# Revit family: REEDEN 3W_LZ68G14WW
name_source: partatom
category: Luminarias
units: mm (PartAtom-declared; Revit-internal decimal feet)

## family parameters
Compartido = No
Corte con vacíos al cargar = No
Cota de conector redondo = Diámetro de uso
Origen de luz = Sí
Punto de cálculo de habitación = No
Se basa en plano de trabajo = Sí
Siempre vertical = No
Tipo de pieza = Normal

## types (1)
- REEDEN 3W_LZ68G14WW
    Cambio de temperatura de color de luz atenuada = <Ninguno>
    Comentarios de vataje = 90-240V
    Descripción = LUMINARIA DE PIE DISPONIBLE A UNA ALTURA DE 400MM CON CUERPO DE ALUMINIO Y VIDRIO, IP 54 USO PARA INTERIORES CON UN PESO DE 1.1KG, CUENTA CON 1 LED CITIZEN CON UNA POTENCIA TOTAL DE 4W, A UNA TEMPERATURA EN BLANCO CALIDO 3000K CON 203 LUMENES, EFICIENCIA DE 50.75LM/W, IRC 80, APERTURA A 120 GRADOS EN STOCK, 0.05mA EN CORRIENTE DE OPERACIÓN, ALIMENTADA A 90-240V.
    Elevación por defecto = 0 mm  [stored 0 ft]
    Fabricante = BRILLANT
    Filtro de color = 16777215
    Longitud de símbolo de origen de luz = 100 mm  [stored 0.328084 ft]
    Lámpara = CITIZEN
    Modelo = LZ68G14WW
    Watt per fixture = 4
    Ángulo de campo de foco = 90.00°
    Ángulo de enfoque = 30.00°
    Ángulo de inclinación = 90.00°

note: [stored X ft] marks values corroborated as IEEE doubles in the binary element streams (Revit-internal decimal feet)

## geometry (parser evidence)
native form markers: Blend x2
no freeform markers — native parametric forms only
